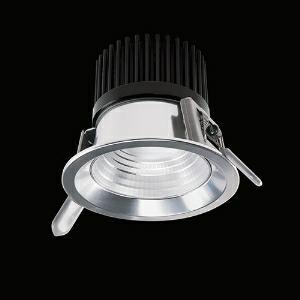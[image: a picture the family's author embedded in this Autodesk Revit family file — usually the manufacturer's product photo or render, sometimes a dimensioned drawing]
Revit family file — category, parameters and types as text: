
# Revit family: spectral_myral_myral_4500-830-f-dali
name_source: partatom
category: Lighting Fixtures
revit_build: Autodesk Revit 2016 (Build: 20150220_1215(x64)
units: mm (PartAtom-declared; Revit-internal decimal feet)

## family parameters
Cut with Voids When Loaded = No
Host = Face
Light Source = No
Part Type = Normal
Room Calculation Point = No
Round Connector Dimension = Use Diameter
Shared = No

## types (1)
- SPECTRAL MYRAL (1 x )
    Apparent Load = 0 VA
    Approval mark = CE
    CIE Flux Codes = 81 99 100 100 100
    Control Gear = Electronic transformer
    Default Elevation = 1800 mm
    Description = SPG0330188
MYRAL recessed spot

Design:
    Height = 0 mm  [stored 0 ft]
    Lamp = 1 x
    Lamp count = 1
    Length = 120 mm
    Luminous efficacy = 0 lm/W
    Manufacturer = Ridi
    ModVariant = No
    Model = MYRAL 4500-830-F-DALI
    Mounting Place = Ceiling
    Mounting Type = Recessed
    Number of Poles = 1
    OnlyDefault = Yes
    Power Factor = 1
    Product Name = SPECTRAL MYRAL
    Product group = Downlight recessed
    ProductGroupID = 400
    Protection Class = Protection class
    Protection Degree = IP 20
    RlxData = <blob elided: 38909 chars, md5=26a4e07f>
    Socket = socket
    Standby Power = 0 W
    System Light Flux = 0 lm
    System Power = 0 W
    Type Image = myral_04.jpg
    URL = http://reluxnet.relux.com
    VarID = ---
    Voltage = 0 V
    Weight = 0.00 kg
    Width = 0 mm  [stored 0 ft]

note: [stored X ft] marks values corroborated as IEEE doubles in the binary element streams (Revit-internal decimal feet)

## geometry (parser evidence)
native form markers: Sweep x9
no freeform markers — native parametric forms only
